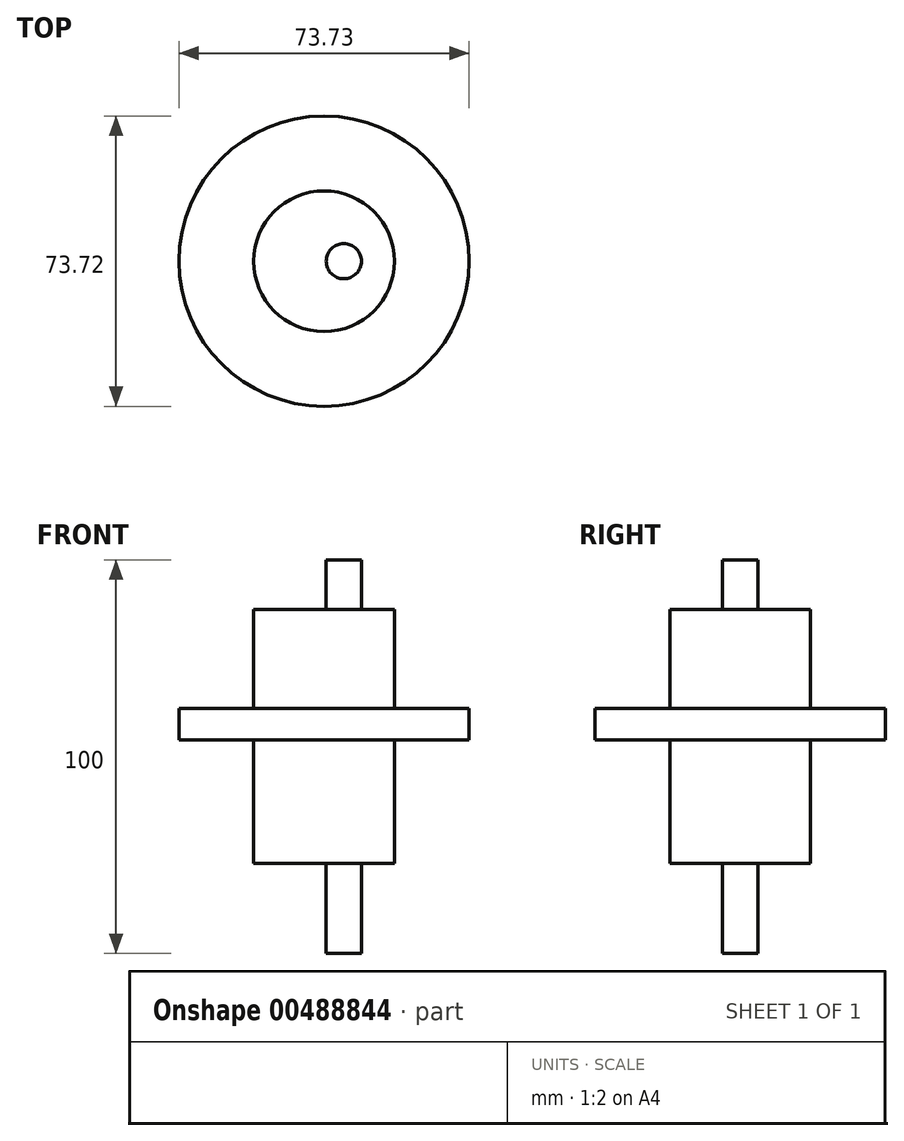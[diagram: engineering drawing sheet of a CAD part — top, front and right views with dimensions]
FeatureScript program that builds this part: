
annotation { "Feature Type Name" : "Feature", "Feature Type Description" : "" }
export const myFeature = defineFeature(function(context is Context, id is Id, definition is map)
    precondition{}
    {
        {
            var Q0;
            Q0=qCreatedBy(makeId("Top.planeOp"),FACE);
            var sketch = newSketch(context, id + "F0", { "sketchPlane" : qUnion([Q0])});
            skCircle(sketch, "E0", {"center": v(0, 0) * mm, "radius": 4.47 * mm});
            skSolve(sketch);
        }
        {
            var Q0;
            Q0 = qSketchRegion(id + "F0", true);
            extrude(context, id + "F1", {"entities" : qUnion([Q0]), "endBound" : BoundingType.SYMMETRIC, "depth" : 100 * mm});
        }
        {
            var Q0;
            Q0=qCreatedBy(makeId("Front.planeOp"),FACE);
            var sketch = newSketch(context, id + "F2", { "sketchPlane" : qUnion([Q0])});
            skLineSegment(sketch, "E1", {"start": v(-5.03, 37.42) * mm, "end": v(-22.9, 37.42) * mm});
            skLineSegment(sketch, "E2", {"start": v(-22.9, 37.42) * mm, "end": v(-22.9, 12.29) * mm});
            skLineSegment(sketch, "E3", {"start": v(-22.9, -27.09) * mm, "end": v(-5.03, -27.09) * mm});
            skLineSegment(sketch, "E4", {"start": v(-5.03, 37.42) * mm, "end": v(-5.03, -27.09) * mm});
            skLineSegment(sketch, "E5", {"start": v(-22.9, 12.29) * mm, "end": v(-41.89, 12.29) * mm});
            skLineSegment(sketch, "E6", {"start": v(-41.89, 12.29) * mm, "end": v(-41.89, 4.19) * mm});
            skLineSegment(sketch, "E7", {"start": v(-41.89, 4.19) * mm, "end": v(-22.9, 4.19) * mm});
            skLineSegment(sketch, "E8.trimOffspring", {"start": v(-22.9, 4.19) * mm, "end": v(-22.9, -27.09) * mm});
            skSolve(sketch);
        }
        {
            var Q0;
            Q0=makeQuery(id+"F2.imprint","IMPRINT",FACE,{"disambiguationData":[TD([[makeQuery(id+"F2.imprint","IMPRINT",EDGE,{"derivedFrom":sQuery(id+"F2.wireOp",EDGE,"E1")}),1.0]])]});
            var Q1;
            Q1=sQuery(id+"F2.wireOp",EDGE,"E4");
            revolve(context, id + "F3", {"operationType" : NewBodyOperationType.ADD, "entities" : qUnion([Q0]), "axis" : qUnion([Q1]), "revolveType" : RevolveType.FULL});
        }
    });
